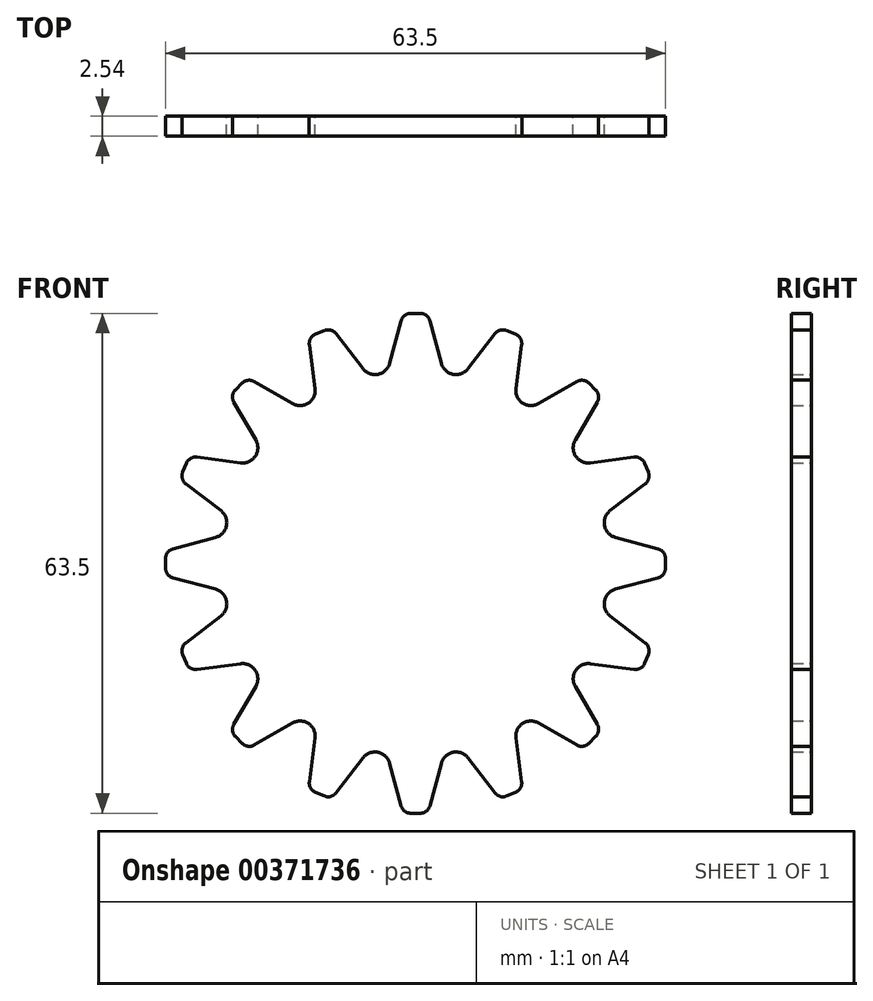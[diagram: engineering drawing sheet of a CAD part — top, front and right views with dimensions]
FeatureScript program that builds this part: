
annotation { "Feature Type Name" : "Feature", "Feature Type Description" : "" }
export const myFeature = defineFeature(function(context is Context, id is Id, definition is map)
    precondition{}
    {
        {
            var Q0;
            Q0=qCreatedBy(makeId("Front.planeOp"),FACE);
            var sketch = newSketch(context, id + "F0", { "sketchPlane" : qUnion([Q0])});
            skCircle(sketch, "E0", {"center": v(0, 0) * mm, "radius": 25.4 * mm, "construction": true});
            skLineSegment(sketch, "E1", {"start": v(0, 0) * mm, "end": v(0, 45.35) * mm, "construction": true});
            skLineSegment(sketch, "E2", {"start": v(-3.29, 25.4) * mm, "end": v(-1.84, 30.8) * mm});
            skLineSegment(sketch, "E3", {"start": v(-0.61, 31.75) * mm, "end": v(0, 31.75) * mm});
            skPoint(sketch, "E4.visualSharp", {"position": v(-1.59, 31.75) * mm});
            skArc(sketch, "E4.filletArc", {"start": v(-0.61, 31.75) * mm, "mid": v(-1.39, 31.49) * mm, "end": v(-1.84, 30.8) * mm});
            skLineSegment(sketch, "E5.MirrorCS", {"start": v(3.29, 25.4) * mm, "end": v(1.84, 30.8) * mm});
            skLineSegment(sketch, "E6.MirrorCS", {"start": v(0.61, 31.75) * mm, "end": v(0, 31.75) * mm});
            skArc(sketch, "E7.MirrorCS", {"start": v(0.61, 31.75) * mm, "mid": v(1.39, 31.49) * mm, "end": v(1.84, 30.8) * mm});
            skPoint(sketch, "E8.MirrorP", {"position": v(1.59, 31.75) * mm});
            skArc(sketch, "E9", {"start": v(3.29, 25.4) * mm, "mid": v(4.78, 24) * mm, "end": v(6.68, 24.73) * mm});
            skPoint(sketch, "E10.1.0", {"position": v(-13.62, 28.73) * mm});
            skLineSegment(sketch, "E10.1.1", {"start": v(-6.68, 24.73) * mm, "end": v(-10.1, 29.17) * mm});
            skLineSegment(sketch, "E10.1.2", {"start": v(-12.76, 22.2) * mm, "end": v(-13.49, 27.76) * mm});
            skPoint(sketch, "E10.1.3", {"position": v(-10.68, 29.94) * mm});
            skArc(sketch, "E10.1.4", {"start": v(-6.68, 24.73) * mm, "mid": v(-4.78, 24) * mm, "end": v(-3.29, 25.4) * mm});
            skArc(sketch, "E10.1.5", {"start": v(-12.72, 29.1) * mm, "mid": v(-13.33, 28.56) * mm, "end": v(-13.49, 27.76) * mm});
            skLineSegment(sketch, "E10.1.6", {"start": v(-12.72, 29.1) * mm, "end": v(-12.15, 29.33) * mm});
            skLineSegment(sketch, "E10.1.7", {"start": v(-11.58, 29.57) * mm, "end": v(-12.15, 29.33) * mm});
            skArc(sketch, "E10.1.8", {"start": v(-11.58, 29.57) * mm, "mid": v(-10.77, 29.62) * mm, "end": v(-10.1, 29.17) * mm});
            skPoint(sketch, "E10.2.0", {"position": v(-23.57, 21.33) * mm});
            skLineSegment(sketch, "E10.2.1", {"start": v(-15.63, 20.29) * mm, "end": v(-20.48, 23.09) * mm});
            skLineSegment(sketch, "E10.2.2", {"start": v(-20.29, 15.63) * mm, "end": v(-23.09, 20.48) * mm});
            skPoint(sketch, "E10.2.3", {"position": v(-21.33, 23.57) * mm});
            skArc(sketch, "E10.2.4", {"start": v(-15.63, 20.29) * mm, "mid": v(-13.6, 20.35) * mm, "end": v(-12.76, 22.2) * mm});
            skArc(sketch, "E10.2.5", {"start": v(-22.88, 22.02) * mm, "mid": v(-23.25, 21.28) * mm, "end": v(-23.09, 20.48) * mm});
            skLineSegment(sketch, "E10.2.6", {"start": v(-22.88, 22.02) * mm, "end": v(-22.45, 22.45) * mm});
            skLineSegment(sketch, "E10.2.7", {"start": v(-22.02, 22.88) * mm, "end": v(-22.45, 22.45) * mm});
            skArc(sketch, "E10.2.8", {"start": v(-22.02, 22.88) * mm, "mid": v(-21.28, 23.25) * mm, "end": v(-20.48, 23.09) * mm});
            skPoint(sketch, "E10.3.0", {"position": v(-29.94, 10.68) * mm});
            skLineSegment(sketch, "E10.3.1", {"start": v(-22.2, 12.76) * mm, "end": v(-27.76, 13.49) * mm});
            skLineSegment(sketch, "E10.3.2", {"start": v(-24.73, 6.68) * mm, "end": v(-29.17, 10.1) * mm});
            skPoint(sketch, "E10.3.3", {"position": v(-28.73, 13.62) * mm});
            skArc(sketch, "E10.3.4", {"start": v(-22.2, 12.76) * mm, "mid": v(-20.35, 13.6) * mm, "end": v(-20.29, 15.63) * mm});
            skArc(sketch, "E10.3.5", {"start": v(-29.57, 11.58) * mm, "mid": v(-29.62, 10.77) * mm, "end": v(-29.17, 10.1) * mm});
            skLineSegment(sketch, "E10.3.6", {"start": v(-29.57, 11.58) * mm, "end": v(-29.33, 12.15) * mm});
            skLineSegment(sketch, "E10.3.7", {"start": v(-29.1, 12.72) * mm, "end": v(-29.33, 12.15) * mm});
            skArc(sketch, "E10.3.8", {"start": v(-29.1, 12.72) * mm, "mid": v(-28.56, 13.33) * mm, "end": v(-27.76, 13.49) * mm});
            skPoint(sketch, "E10.4.0", {"position": v(-31.75, -1.59) * mm});
            skLineSegment(sketch, "E10.4.1", {"start": v(-25.4, 3.29) * mm, "end": v(-30.8, 1.84) * mm});
            skLineSegment(sketch, "E10.4.2", {"start": v(-25.4, -3.29) * mm, "end": v(-30.8, -1.84) * mm});
            skPoint(sketch, "E10.4.3", {"position": v(-31.75, 1.59) * mm});
            skArc(sketch, "E10.4.4", {"start": v(-25.4, 3.29) * mm, "mid": v(-24, 4.78) * mm, "end": v(-24.73, 6.68) * mm});
            skArc(sketch, "E10.4.5", {"start": v(-31.75, -0.61) * mm, "mid": v(-31.49, -1.39) * mm, "end": v(-30.8, -1.84) * mm});
            skLineSegment(sketch, "E10.4.6", {"start": v(-31.75, -0.61) * mm, "end": v(-31.75, 0) * mm});
            skLineSegment(sketch, "E10.4.7", {"start": v(-31.75, 0.61) * mm, "end": v(-31.75, 0) * mm});
            skArc(sketch, "E10.4.8", {"start": v(-31.75, 0.61) * mm, "mid": v(-31.49, 1.39) * mm, "end": v(-30.8, 1.84) * mm});
            skPoint(sketch, "E10.5.0", {"position": v(-28.73, -13.62) * mm});
            skLineSegment(sketch, "E10.5.1", {"start": v(-24.73, -6.68) * mm, "end": v(-29.17, -10.1) * mm});
            skLineSegment(sketch, "E10.5.2", {"start": v(-22.2, -12.76) * mm, "end": v(-27.76, -13.49) * mm});
            skPoint(sketch, "E10.5.3", {"position": v(-29.94, -10.68) * mm});
            skArc(sketch, "E10.5.4", {"start": v(-24.73, -6.68) * mm, "mid": v(-24, -4.78) * mm, "end": v(-25.4, -3.29) * mm});
            skArc(sketch, "E10.5.5", {"start": v(-29.1, -12.72) * mm, "mid": v(-28.56, -13.33) * mm, "end": v(-27.76, -13.49) * mm});
            skLineSegment(sketch, "E10.5.6", {"start": v(-29.1, -12.72) * mm, "end": v(-29.33, -12.15) * mm});
            skLineSegment(sketch, "E10.5.7", {"start": v(-29.57, -11.58) * mm, "end": v(-29.33, -12.15) * mm});
            skArc(sketch, "E10.5.8", {"start": v(-29.57, -11.58) * mm, "mid": v(-29.62, -10.77) * mm, "end": v(-29.17, -10.1) * mm});
            skPoint(sketch, "E10.6.0", {"position": v(-21.33, -23.57) * mm});
            skLineSegment(sketch, "E10.6.1", {"start": v(-20.29, -15.63) * mm, "end": v(-23.09, -20.48) * mm});
            skLineSegment(sketch, "E10.6.2", {"start": v(-15.63, -20.29) * mm, "end": v(-20.48, -23.09) * mm});
            skPoint(sketch, "E10.6.3", {"position": v(-23.57, -21.33) * mm});
            skArc(sketch, "E10.6.4", {"start": v(-20.29, -15.63) * mm, "mid": v(-20.35, -13.6) * mm, "end": v(-22.2, -12.76) * mm});
            skArc(sketch, "E10.6.5", {"start": v(-22.02, -22.88) * mm, "mid": v(-21.28, -23.25) * mm, "end": v(-20.48, -23.09) * mm});
            skLineSegment(sketch, "E10.6.6", {"start": v(-22.02, -22.88) * mm, "end": v(-22.45, -22.45) * mm});
            skLineSegment(sketch, "E10.6.7", {"start": v(-22.88, -22.02) * mm, "end": v(-22.45, -22.45) * mm});
            skArc(sketch, "E10.6.8", {"start": v(-22.88, -22.02) * mm, "mid": v(-23.25, -21.28) * mm, "end": v(-23.09, -20.48) * mm});
            skPoint(sketch, "E10.7.0", {"position": v(-10.68, -29.94) * mm});
            skLineSegment(sketch, "E10.7.1", {"start": v(-12.76, -22.2) * mm, "end": v(-13.49, -27.76) * mm});
            skLineSegment(sketch, "E10.7.2", {"start": v(-6.68, -24.73) * mm, "end": v(-10.1, -29.17) * mm});
            skPoint(sketch, "E10.7.3", {"position": v(-13.62, -28.73) * mm});
            skArc(sketch, "E10.7.4", {"start": v(-12.76, -22.2) * mm, "mid": v(-13.6, -20.35) * mm, "end": v(-15.63, -20.29) * mm});
            skArc(sketch, "E10.7.5", {"start": v(-11.58, -29.57) * mm, "mid": v(-10.77, -29.62) * mm, "end": v(-10.1, -29.17) * mm});
            skLineSegment(sketch, "E10.7.6", {"start": v(-11.58, -29.57) * mm, "end": v(-12.15, -29.33) * mm});
            skLineSegment(sketch, "E10.7.7", {"start": v(-12.72, -29.1) * mm, "end": v(-12.15, -29.33) * mm});
            skArc(sketch, "E10.7.8", {"start": v(-12.72, -29.1) * mm, "mid": v(-13.33, -28.56) * mm, "end": v(-13.49, -27.76) * mm});
            skPoint(sketch, "E10.8.0", {"position": v(1.59, -31.75) * mm});
            skLineSegment(sketch, "E10.8.1", {"start": v(-3.29, -25.4) * mm, "end": v(-1.84, -30.8) * mm});
            skLineSegment(sketch, "E10.8.2", {"start": v(3.29, -25.4) * mm, "end": v(1.84, -30.8) * mm});
            skPoint(sketch, "E10.8.3", {"position": v(-1.59, -31.75) * mm});
            skArc(sketch, "E10.8.4", {"start": v(-3.29, -25.4) * mm, "mid": v(-4.78, -24) * mm, "end": v(-6.68, -24.73) * mm});
            skArc(sketch, "E10.8.5", {"start": v(0.61, -31.75) * mm, "mid": v(1.39, -31.49) * mm, "end": v(1.84, -30.8) * mm});
            skLineSegment(sketch, "E10.8.6", {"start": v(0.61, -31.75) * mm, "end": v(0, -31.75) * mm});
            skLineSegment(sketch, "E10.8.7", {"start": v(-0.61, -31.75) * mm, "end": v(0, -31.75) * mm});
            skArc(sketch, "E10.8.8", {"start": v(-0.61, -31.75) * mm, "mid": v(-1.39, -31.49) * mm, "end": v(-1.84, -30.8) * mm});
            skPoint(sketch, "E10.9.0", {"position": v(13.62, -28.73) * mm});
            skLineSegment(sketch, "E10.9.1", {"start": v(6.68, -24.73) * mm, "end": v(10.1, -29.17) * mm});
            skLineSegment(sketch, "E10.9.2", {"start": v(12.76, -22.2) * mm, "end": v(13.49, -27.76) * mm});
            skPoint(sketch, "E10.9.3", {"position": v(10.68, -29.94) * mm});
            skArc(sketch, "E10.9.4", {"start": v(6.68, -24.73) * mm, "mid": v(4.78, -24) * mm, "end": v(3.29, -25.4) * mm});
            skArc(sketch, "E10.9.5", {"start": v(12.72, -29.1) * mm, "mid": v(13.33, -28.56) * mm, "end": v(13.49, -27.76) * mm});
            skLineSegment(sketch, "E10.9.6", {"start": v(12.72, -29.1) * mm, "end": v(12.15, -29.33) * mm});
            skLineSegment(sketch, "E10.9.7", {"start": v(11.58, -29.57) * mm, "end": v(12.15, -29.33) * mm});
            skArc(sketch, "E10.9.8", {"start": v(11.58, -29.57) * mm, "mid": v(10.77, -29.62) * mm, "end": v(10.1, -29.17) * mm});
            skPoint(sketch, "E10.10.0", {"position": v(23.57, -21.33) * mm});
            skLineSegment(sketch, "E10.10.1", {"start": v(15.63, -20.29) * mm, "end": v(20.48, -23.09) * mm});
            skLineSegment(sketch, "E10.10.2", {"start": v(20.29, -15.63) * mm, "end": v(23.09, -20.48) * mm});
            skPoint(sketch, "E10.10.3", {"position": v(21.33, -23.57) * mm});
            skArc(sketch, "E10.10.4", {"start": v(15.63, -20.29) * mm, "mid": v(13.6, -20.35) * mm, "end": v(12.76, -22.2) * mm});
            skArc(sketch, "E10.10.5", {"start": v(22.88, -22.02) * mm, "mid": v(23.25, -21.28) * mm, "end": v(23.09, -20.48) * mm});
            skLineSegment(sketch, "E10.10.6", {"start": v(22.88, -22.02) * mm, "end": v(22.45, -22.45) * mm});
            skLineSegment(sketch, "E10.10.7", {"start": v(22.02, -22.88) * mm, "end": v(22.45, -22.45) * mm});
            skArc(sketch, "E10.10.8", {"start": v(22.02, -22.88) * mm, "mid": v(21.28, -23.25) * mm, "end": v(20.48, -23.09) * mm});
            skPoint(sketch, "E10.11.0", {"position": v(29.94, -10.68) * mm});
            skLineSegment(sketch, "E10.11.1", {"start": v(22.2, -12.76) * mm, "end": v(27.76, -13.49) * mm});
            skLineSegment(sketch, "E10.11.2", {"start": v(24.73, -6.68) * mm, "end": v(29.17, -10.1) * mm});
            skPoint(sketch, "E10.11.3", {"position": v(28.73, -13.62) * mm});
            skArc(sketch, "E10.11.4", {"start": v(22.2, -12.76) * mm, "mid": v(20.35, -13.6) * mm, "end": v(20.29, -15.63) * mm});
            skArc(sketch, "E10.11.5", {"start": v(29.57, -11.58) * mm, "mid": v(29.62, -10.77) * mm, "end": v(29.17, -10.1) * mm});
            skLineSegment(sketch, "E10.11.6", {"start": v(29.57, -11.58) * mm, "end": v(29.33, -12.15) * mm});
            skLineSegment(sketch, "E10.11.7", {"start": v(29.1, -12.72) * mm, "end": v(29.33, -12.15) * mm});
            skArc(sketch, "E10.11.8", {"start": v(29.1, -12.72) * mm, "mid": v(28.56, -13.33) * mm, "end": v(27.76, -13.49) * mm});
            skPoint(sketch, "E10.12.0", {"position": v(31.75, 1.59) * mm});
            skLineSegment(sketch, "E10.12.1", {"start": v(25.4, -3.29) * mm, "end": v(30.8, -1.84) * mm});
            skLineSegment(sketch, "E10.12.2", {"start": v(25.4, 3.29) * mm, "end": v(30.8, 1.84) * mm});
            skPoint(sketch, "E10.12.3", {"position": v(31.75, -1.59) * mm});
            skArc(sketch, "E10.12.4", {"start": v(25.4, -3.29) * mm, "mid": v(24, -4.78) * mm, "end": v(24.73, -6.68) * mm});
            skArc(sketch, "E10.12.5", {"start": v(31.75, 0.61) * mm, "mid": v(31.49, 1.39) * mm, "end": v(30.8, 1.84) * mm});
            skLineSegment(sketch, "E10.12.6", {"start": v(31.75, 0.61) * mm, "end": v(31.75, 0) * mm});
            skLineSegment(sketch, "E10.12.7", {"start": v(31.75, -0.61) * mm, "end": v(31.75, 0) * mm});
            skArc(sketch, "E10.12.8", {"start": v(31.75, -0.61) * mm, "mid": v(31.49, -1.39) * mm, "end": v(30.8, -1.84) * mm});
            skPoint(sketch, "E10.13.0", {"position": v(28.73, 13.62) * mm});
            skLineSegment(sketch, "E10.13.1", {"start": v(24.73, 6.68) * mm, "end": v(29.17, 10.1) * mm});
            skLineSegment(sketch, "E10.13.2", {"start": v(22.2, 12.76) * mm, "end": v(27.76, 13.49) * mm});
            skPoint(sketch, "E10.13.3", {"position": v(29.94, 10.68) * mm});
            skArc(sketch, "E10.13.4", {"start": v(24.73, 6.68) * mm, "mid": v(24, 4.78) * mm, "end": v(25.4, 3.29) * mm});
            skArc(sketch, "E10.13.5", {"start": v(29.1, 12.72) * mm, "mid": v(28.56, 13.33) * mm, "end": v(27.76, 13.49) * mm});
            skLineSegment(sketch, "E10.13.6", {"start": v(29.1, 12.72) * mm, "end": v(29.33, 12.15) * mm});
            skLineSegment(sketch, "E10.13.7", {"start": v(29.57, 11.58) * mm, "end": v(29.33, 12.15) * mm});
            skArc(sketch, "E10.13.8", {"start": v(29.57, 11.58) * mm, "mid": v(29.62, 10.77) * mm, "end": v(29.17, 10.1) * mm});
            skPoint(sketch, "E10.14.0", {"position": v(21.33, 23.57) * mm});
            skLineSegment(sketch, "E10.14.1", {"start": v(20.29, 15.63) * mm, "end": v(23.09, 20.48) * mm});
            skLineSegment(sketch, "E10.14.2", {"start": v(15.63, 20.29) * mm, "end": v(20.48, 23.09) * mm});
            skPoint(sketch, "E10.14.3", {"position": v(23.57, 21.33) * mm});
            skArc(sketch, "E10.14.4", {"start": v(20.29, 15.63) * mm, "mid": v(20.35, 13.6) * mm, "end": v(22.2, 12.76) * mm});
            skArc(sketch, "E10.14.5", {"start": v(22.02, 22.88) * mm, "mid": v(21.28, 23.25) * mm, "end": v(20.48, 23.09) * mm});
            skLineSegment(sketch, "E10.14.6", {"start": v(22.02, 22.88) * mm, "end": v(22.45, 22.45) * mm});
            skLineSegment(sketch, "E10.14.7", {"start": v(22.88, 22.02) * mm, "end": v(22.45, 22.45) * mm});
            skArc(sketch, "E10.14.8", {"start": v(22.88, 22.02) * mm, "mid": v(23.25, 21.28) * mm, "end": v(23.09, 20.48) * mm});
            skPoint(sketch, "E10.15.0", {"position": v(10.68, 29.94) * mm});
            skLineSegment(sketch, "E10.15.1", {"start": v(12.76, 22.2) * mm, "end": v(13.49, 27.76) * mm});
            skLineSegment(sketch, "E10.15.2", {"start": v(6.68, 24.73) * mm, "end": v(10.1, 29.17) * mm});
            skPoint(sketch, "E10.15.3", {"position": v(13.62, 28.73) * mm});
            skArc(sketch, "E10.15.4", {"start": v(12.76, 22.2) * mm, "mid": v(13.6, 20.35) * mm, "end": v(15.63, 20.29) * mm});
            skArc(sketch, "E10.15.5", {"start": v(11.58, 29.57) * mm, "mid": v(10.77, 29.62) * mm, "end": v(10.1, 29.17) * mm});
            skLineSegment(sketch, "E10.15.6", {"start": v(11.58, 29.57) * mm, "end": v(12.15, 29.33) * mm});
            skLineSegment(sketch, "E10.15.7", {"start": v(12.72, 29.1) * mm, "end": v(12.15, 29.33) * mm});
            skArc(sketch, "E10.15.8", {"start": v(12.72, 29.1) * mm, "mid": v(13.33, 28.56) * mm, "end": v(13.49, 27.76) * mm});
            skSolve(sketch);
        }
        {
            var Q0;
            Q0 = qSketchRegion(id + "F0", true);
            var Q1;
            Q1=makeQuery(id+"F0.imprint","IMPRINT",FACE,{"disambiguationData":[TD([[makeQuery(id+"F0.imprint","IMPRINT",EDGE,{"derivedFrom":sQuery(id+"F0.wireOp",EDGE,"E2")}),-1.0]])]});
            extrude(context, id + "F1", {"entities" : qUnion([Q0, Q1]), "depth" : 2.54 * mm});
        }
    });
